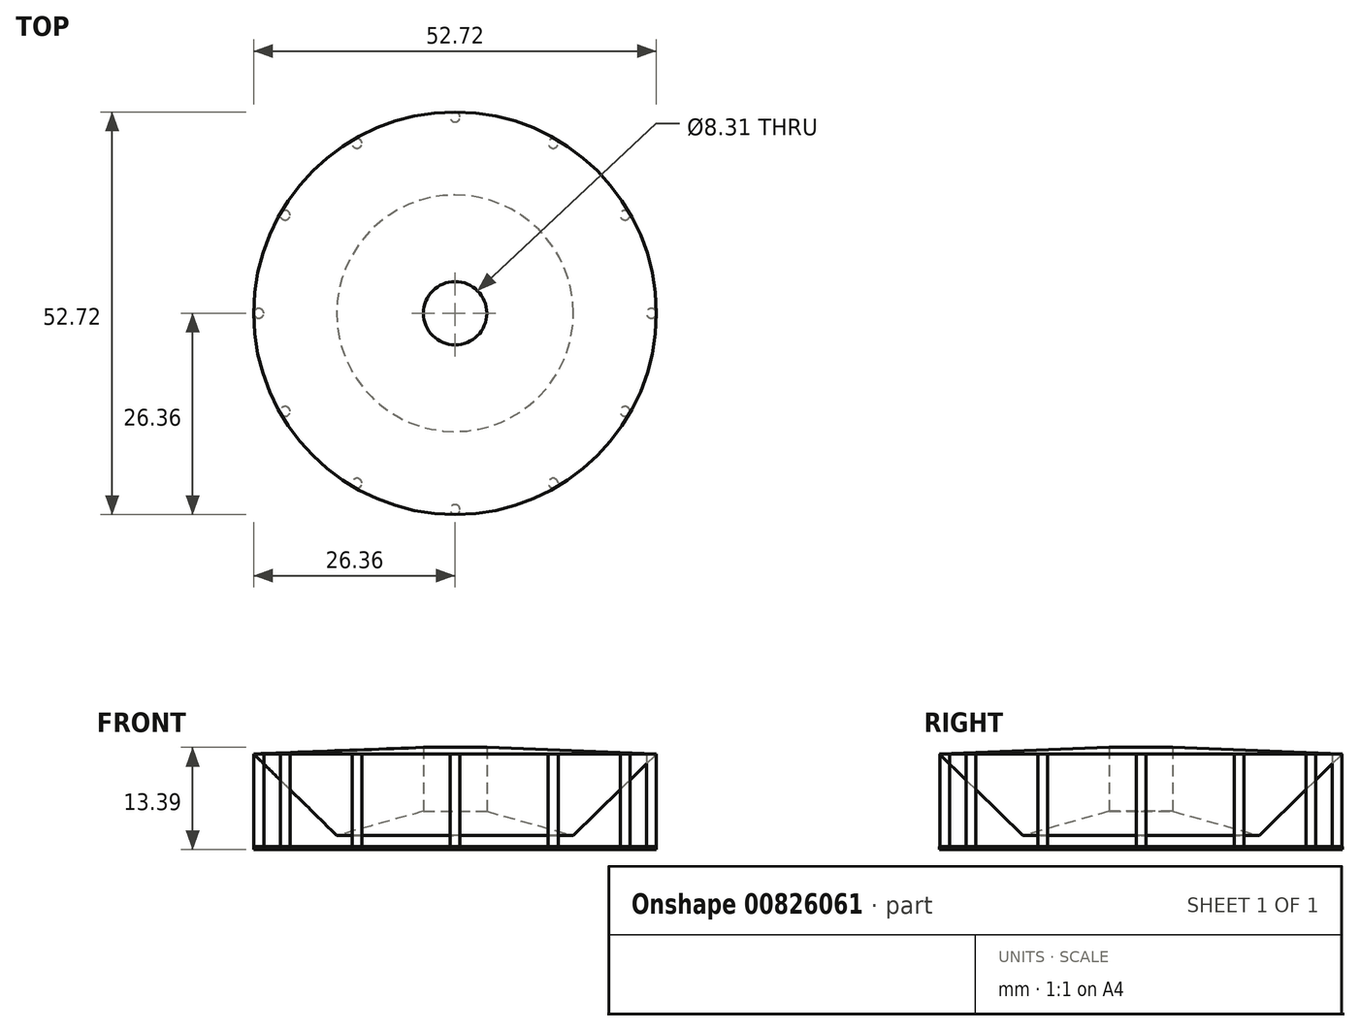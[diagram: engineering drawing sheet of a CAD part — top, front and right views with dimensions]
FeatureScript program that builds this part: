
annotation { "Feature Type Name" : "Feature", "Feature Type Description" : "" }
export const myFeature = defineFeature(function(context is Context, id is Id, definition is map)
    precondition{}
    {
        {
            var Q0;
            Q0=qCreatedBy(makeId("Right.planeOp"),FACE);
            var sketch = newSketch(context, id + "F0", { "sketchPlane" : qUnion([Q0])});
            skLineSegment(sketch, "E0", {"start": v(0, 0) * mm, "end": v(15.5, 0) * mm});
            skLineSegment(sketch, "E1", {"start": v(0, 0) * mm, "end": v(0, 4.6) * mm});
            skLineSegment(sketch, "E2", {"start": v(0, 4.6) * mm, "end": v(4.15, 4.6) * mm});
            skLineSegment(sketch, "E3", {"start": v(4.15, 4.6) * mm, "end": v(4.15, 12.98) * mm});
            skLineSegment(sketch, "E4", {"start": v(15.5, 1.44) * mm, "end": v(26.36, 12.12) * mm});
            skLineSegment(sketch, "E5", {"start": v(26.36, 12.12) * mm, "end": v(4.15, 12.98) * mm});
            skLineSegment(sketch, "E6", {"start": v(4.15, 4.6) * mm, "end": v(15.5, 1.44) * mm});
            skLineSegment(sketch, "E7", {"start": v(26.36, 0) * mm, "end": v(15.5, 0) * mm});
            skLineSegment(sketch, "E8", {"start": v(26.36, 0) * mm, "end": v(26.36, -0.41) * mm});
            skLineSegment(sketch, "E9", {"start": v(26.36, -0.41) * mm, "end": v(0, -0.41) * mm});
            skLineSegment(sketch, "E10", {"start": v(0, 0) * mm, "end": v(0, -0.41) * mm});
            skSolve(sketch);
        }
        {
            var Q0;
            Q0=makeQuery(id+"F0.imprint","IMPRINT",FACE,{"disambiguationData":[TD([[makeQuery(id+"F0.imprint","IMPRINT",EDGE,{"derivedFrom":sQuery(id+"F0.wireOp",EDGE,"E3")}),-1.0]])]});
            var Q1;
            Q1=makeQuery(id+"F0.imprint","IMPRINT",FACE,{"disambiguationData":[TD([[makeQuery(id+"F0.imprint","IMPRINT",EDGE,{"derivedFrom":sQuery(id+"F0.wireOp",EDGE,"E0")}),-1.0]])]});
            var Q2;
            Q2=sQuery(id+"F0.wireOp",EDGE,"E1");
            revolve(context, id + "F1", {"surfaceOperationType" : NewSurfaceOperationType.NEW, "entities" : qUnion([Q0, Q1]), "axis" : qUnion([Q2]), "revolveType" : RevolveType.FULL});
        }
        {
            var Q0;
            Q0=qCreatedBy(makeId("Top.planeOp"),FACE);
            var sketch = newSketch(context, id + "F2", { "sketchPlane" : qUnion([Q0])});
            skCircle(sketch, "E11", {"center": v(0, 25.7) * mm, "radius": 0.64 * mm});
            skCircle(sketch, "E12.1.0", {"center": v(-12.85, 22.25) * mm, "radius": 0.64 * mm});
            skCircle(sketch, "E12.2.0", {"center": v(-22.25, 12.85) * mm, "radius": 0.64 * mm});
            skCircle(sketch, "E12.3.0", {"center": v(-25.7, 0) * mm, "radius": 0.64 * mm});
            skCircle(sketch, "E12.4.0", {"center": v(-22.25, -12.85) * mm, "radius": 0.64 * mm});
            skCircle(sketch, "E12.5.0", {"center": v(-12.85, -22.25) * mm, "radius": 0.64 * mm});
            skCircle(sketch, "E12.6.0", {"center": v(0, -25.7) * mm, "radius": 0.64 * mm});
            skCircle(sketch, "E12.7.0", {"center": v(12.85, -22.25) * mm, "radius": 0.64 * mm});
            skCircle(sketch, "E12.8.0", {"center": v(22.25, -12.85) * mm, "radius": 0.64 * mm});
            skCircle(sketch, "E12.9.0", {"center": v(25.7, 0) * mm, "radius": 0.64 * mm});
            skCircle(sketch, "E12.10.0", {"center": v(22.25, 12.85) * mm, "radius": 0.64 * mm});
            skCircle(sketch, "E12.11.0", {"center": v(12.85, 22.25) * mm, "radius": 0.64 * mm});
            skPoint(sketch, "E12.center", {"position": v(0, 0) * mm});
            skSolve(sketch);
        }
        {
            var Q0;
            Q0 = qSketchRegion(id + "F2", true);
            extrude(context, id + "F3", {"entities" : qUnion([Q0]), "depth" : 12.1 * mm, "offsetDistance" : 25 * mm});
        }
    });
